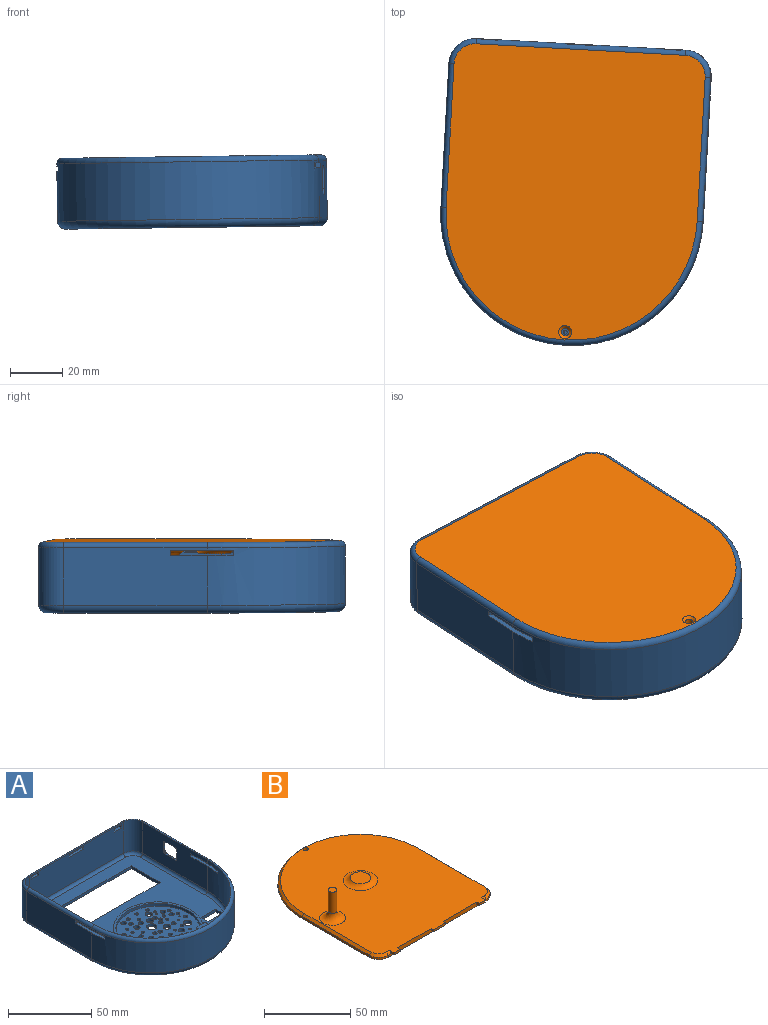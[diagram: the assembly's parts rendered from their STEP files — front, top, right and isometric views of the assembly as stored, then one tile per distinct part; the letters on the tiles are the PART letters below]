
ASSEMBLY  parts=2 mates=1
PART A: 165 faces, bbox 108.2x119.9x27 mm
  f0: plane 55x22mm, normal (1,0,0), area 1042.4mm2, adj f7,f86,f101,f102,f103,f126,f132,f146
  f1: plane 55x23mm, normal (-1,0,0), area 1138.9mm2, adj f8,f92,f101,f102,f103,f120,f132,f138
  f2: plane 20x1.61mm, normal (1,0,0), area 32.1mm2, adj f116,f159,f162,f163
  f3: plane 20x4mm, normal (0,1,0), area 80mm2, adj f116,f156,f159,f160
  f4: plane 20x1.61mm, normal (-1,0,0), area 32.1mm2, adj f116,f154,f156,f157
  f5: plane 80x22mm, normal (0,1,0), area 1733mm2, adj f14,f86,f105,f106,f107,f109,f110,f111
  f6: plane 80x23mm, normal (0,-1,0), area 1789mm2, adj f91,f92,f104,f105,f106,f107,f108,f109
  f7: cylinder r=50mm len=100mm, axis (0,0,-1), area 3415.5mm2, adj f0,f15,f96,f98,f99,f100,f101,f103
  f8: cylinder r=48mm len=96mm, axis (0,0,-1), area 3176.9mm2, adj f1,f9,f96,f98,f99,f100,f101,f103
  f9: plane 55x23mm, normal (1,0,0), area 1237mm2, adj f8,f91,f96,f97,f98,f124,f136
  f10: plane 50.8x50.8mm, normal (0,0,1), area 1631.9mm2, adj f20,f21,f22,f23,f24,f25,f26,f27
  f11: plane 12.3x2mm, normal (0,-1,0), area 24.6mm2, adj f12,f88,f89,f90
  f12: plane 5.9x2mm, normal (-1,0,0), area 11.8mm2, adj f11,f13,f89,f90
  f13: plane 12.3x2mm, normal (0,1,0), area 24.6mm2, adj f12,f88,f89,f90
  f14: cylinder r=10mm len=22mm, axis (0,0,-1), area 345.6mm2, adj f5,f15,f131,f137
  f15: plane 55x22mm, normal (-1,0,0), area 1182mm2, adj f7,f14,f96,f97,f98,f130,f136
  f16: plane 24.5x2mm, normal (1,0,0), area 49mm2, adj f17,f87,f89,f90
  f17: plane 72x2mm, normal (0,-1,0), area 144mm2, adj f16,f18,f89,f90
  f18: plane 24.5x2mm, normal (-1,0,0), area 49mm2, adj f17,f87,f89,f90
  f19: cylinder r=2.5mm len=5mm, axis (0,0,-1), area 31.4mm2, adj f89,f90
  f20: cylinder r=1.09mm len=2.19mm, axis (0,0,-1), area 13.7mm2, adj f10,f90
  f21: cylinder r=1.17mm len=2.34mm, axis (0,0,-1), area 14.7mm2, adj f10,f90
  f22: cylinder r=1.2mm len=2.41mm, axis (0,0,-1), area 15.1mm2, adj f10,f90
  f23: cylinder r=1.12mm len=2.25mm, axis (0,0,-1), area 14.1mm2, adj f10,f90
  f24: cylinder r=1.29mm len=2.57mm, axis (0,0,-1), area 16.2mm2, adj f10,f90
  f25: cylinder r=1.3mm len=2.59mm, axis (0,0,-1), area 16.3mm2, adj f10,f90
  f26: cylinder r=1.3mm len=2.6mm, axis (0,0,-1), area 16.3mm2, adj f10,f90
  f27: cylinder r=1.66mm len=3.33mm, axis (0,0,-1), area 20.9mm2, adj f10,f90
  f28: cylinder r=1.03mm len=2.06mm, axis (0,0,-1), area 12.9mm2, adj f10,f90
  f29: cylinder r=3.5mm len=7mm, axis (0,0,-1), area 44mm2, adj f89,f90
  f30: cylinder r=0.84mm len=2mm, axis (0,0,-1), area 10.6mm2, adj f10,f90
  f31: cylinder r=1.27mm len=2.54mm, axis (0,0,-1), area 15.9mm2, adj f10,f90
  f32: cylinder r=1.09mm len=2.19mm, axis (0,0,-1), area 13.7mm2, adj f10,f90
  f33: cylinder r=1.31mm len=2.61mm, axis (0,0,-1), area 16.4mm2, adj f10,f90
  f34: cylinder r=0.98mm len=2mm, axis (0,0,-1), area 12.3mm2, adj f10,f90
  f35: cylinder r=0.96mm len=2mm, axis (0,0,-1), area 12mm2, adj f10,f90
  f36: cylinder r=1.35mm len=2.7mm, axis (0,0,-1), area 17mm2, adj f10,f90
  f37: cylinder r=0.94mm len=2mm, axis (0,0,-1), area 11.8mm2, adj f10,f90
  f38: cylinder r=2.4mm len=4.79mm, axis (0,0,-1), area 30.1mm2, adj f10,f90
  f39: cylinder r=1.14mm len=2.28mm, axis (0,0,-1), area 14.3mm2, adj f10,f90
  f40: cylinder r=1.19mm len=2.38mm, axis (0,0,-1), area 15mm2, adj f10,f90
  f41: cylinder r=1.46mm len=2.91mm, axis (0,0,-1), area 18.3mm2, adj f10,f90
  f42: cylinder r=1.28mm len=2.56mm, axis (0,0,-1), area 16.1mm2, adj f10,f90
  f43: cylinder r=1.34mm len=2.69mm, axis (0,0,-1), area 16.9mm2, adj f10,f90
  f44: cylinder r=0.79mm len=2mm, axis (0,0,-1), area 9.9mm2, adj f10,f90
  f45: cylinder r=1.96mm len=3.93mm, axis (0,0,-1), area 24.7mm2, adj f10,f90
  f46: cylinder r=1.15mm len=2.3mm, axis (0,0,-1), area 14.5mm2, adj f10,f90
  f47: cylinder r=0.9mm len=2mm, axis (0,0,-1), area 11.3mm2, adj f10,f90
  f48: cylinder r=1.91mm len=3.83mm, axis (0,0,-1), area 24mm2, adj f10,f90
  f49: cylinder r=1.3mm len=2.6mm, axis (0,0,-1), area 16.3mm2, adj f10,f90
  f50: cylinder r=1.04mm len=2.07mm, axis (0,0,-1), area 13mm2, adj f10,f90
  f51: cylinder r=0.35mm len=2mm, axis (0,0,-1), area 4.4mm2, adj f10,f90
  f52: cylinder r=1.46mm len=2.92mm, axis (0,0,-1), area 18.3mm2, adj f10,f90
  f53: cylinder r=0.89mm len=2mm, axis (0,0,-1), area 11.2mm2, adj f10,f90
  f54: cylinder r=1.49mm len=2.98mm, axis (0,0,-1), area 18.7mm2, adj f10,f90
  f55: cylinder r=1.02mm len=2.04mm, axis (0,0,-1), area 12.8mm2, adj f10,f90
  f56: cylinder r=1.22mm len=2.44mm, axis (0,0,-1), area 15.4mm2, adj f10,f90
  f57: cylinder r=1.36mm len=2.73mm, axis (0,0,-1), area 17.1mm2, adj f10,f90
  f58: cylinder r=1.37mm len=2.74mm, axis (0,0,-1), area 17.2mm2, adj f10,f90
  f59: cylinder r=2.62mm len=5.23mm, axis (0,0,-1), area 32.9mm2, adj f10,f90
  f60: cylinder r=0.95mm len=2mm, axis (0,0,-1), area 11.9mm2, adj f10,f90
  f61: cylinder r=1.1mm len=2.2mm, axis (0,0,-1), area 13.8mm2, adj f10,f90
  f62: cylinder r=1.18mm len=2.37mm, axis (0,0,-1), area 14.9mm2, adj f10,f90
  f63: cylinder r=0.85mm len=2mm, axis (0,0,-1), area 10.7mm2, adj f10,f90
  f64: cylinder r=1.19mm len=2.38mm, axis (0,0,-1), area 14.9mm2, adj f10,f90
  f65: cylinder r=0.96mm len=2mm, axis (0,0,-1), area 12mm2, adj f10,f90
  f66: cylinder r=1.7mm len=3.4mm, axis (0,0,-1), area 21.3mm2, adj f10,f90
  f67: cylinder r=0.78mm len=2mm, axis (0,0,-1), area 9.8mm2, adj f10,f90
  f68: cylinder r=0.8mm len=2mm, axis (0,0,-1), area 10.1mm2, adj f10,f90
  f69: cylinder r=1.68mm len=3.36mm, axis (0,0,-1), area 21.1mm2, adj f10,f90
  f70: cylinder r=0.69mm len=2mm, axis (0,0,-1), area 8.7mm2, adj f10,f90
  f71: cylinder r=1.23mm len=2.46mm, axis (0,0,-1), area 15.4mm2, adj f10,f90
  f72: cylinder r=0.88mm len=2mm, axis (0,0,-1), area 11mm2, adj f10,f90
  f73: cylinder r=1.53mm len=3.05mm, axis (0,0,-1), area 19.2mm2, adj f10,f90
  f74: cylinder r=0.9mm len=2mm, axis (0,0,-1), area 11.3mm2, adj f10,f90
  f75: cylinder r=0.63mm len=2mm, axis (0,0,-1), area 7.9mm2, adj f10,f90
  f76: cylinder r=1.17mm len=2.33mm, axis (0,0,-1), area 14.7mm2, adj f10,f90
  f77: cylinder r=1.62mm len=3.25mm, axis (0,0,-1), area 20.4mm2, adj f10,f90
  f78: cylinder r=2.15mm len=4.3mm, axis (0,0,-1), area 27mm2, adj f10,f90
  f79: cylinder r=1.51mm len=3.02mm, axis (0,0,-1), area 19mm2, adj f10,f90
  f80: cylinder r=1.34mm len=2.68mm, axis (0,0,-1), area 16.8mm2, adj f10,f90
  f81: cylinder r=2.36mm len=4.72mm, axis (0,0,-1), area 29.6mm2, adj f10,f90
  f82: cylinder r=3.06mm len=6.12mm, axis (0,0,-1), area 38.5mm2, adj f10,f90
  f83: cylinder r=2.12mm len=4.25mm, axis (0,0,-1), area 26.7mm2, adj f10,f90
  f84: cylinder r=1.85mm len=3.7mm, axis (0,0,-1), area 23.2mm2, adj f10,f90
  f85: cylinder r=1mm len=2mm, axis (0,0,-1), area 12.6mm2, adj f10,f90
  f86: cylinder r=10mm len=22mm, axis (0,0,-1), area 345.6mm2, adj f0,f5,f127,f133
  f87: plane 72x2mm, normal (0,1,0), area 144mm2, adj f16,f18,f89,f90
  f88: plane 5.9x2mm, normal (1,0,0), area 11.8mm2, adj f11,f13,f89,f90
  f89: plane 106.61x92mm, normal (0,0,1), area 4688.8mm2, adj f11,f12,f13,f16,f17,f18,f19,f29
  f90: plane 109x94mm, normal (0,0,-1), area 6987.2mm2, adj f11,f12,f13,f16,f17,f18,f19,f20
  f91: cylinder r=8mm len=23mm, axis (0,0,-1), area 289mm2, adj f6,f9,f123,f137
  f92: cylinder r=8mm len=23mm, axis (0,0,-1), area 289mm2, adj f1,f6,f121,f133
  f93: cylinder r=25.4mm len=50.8mm, axis (0,0,-1), area 319.2mm2, adj f10,f95
  f94: cylinder r=26.9mm len=53.8mm, axis (0,0,-1), area 338mm2, adj f89,f95
  f95: plane 53.8x53.8mm, normal (0,0,1), area 246.5mm2, adj f93,f94
  f96: plane 24x3.05mm, normal (0,0,1), area 48.1mm2, adj f7,f8,f9,f15,f97,f99
  f97: plane 2x2mm, normal (0,-1,0), area 4mm2, adj f9,f15,f96,f98
  f98: plane 24x3.05mm, normal (0,0,-1), area 48.1mm2, adj f7,f8,f9,f15,f97,f99
  f99: plane 2.04x2mm, normal (0,1,0), area 4.1mm2, adj f7,f8,f96,f98
  f100: plane 2.04x2mm, normal (0,1,0), area 4.1mm2, adj f7,f8,f101,f103
  f101: plane 24x3.05mm, normal (0,0,-1), area 48.1mm2, adj f0,f1,f7,f8,f100,f102
  f102: plane 2x2mm, normal (0,-1,0), area 4mm2, adj f0,f1,f101,f103
  f103: plane 24x3.05mm, normal (0,0,1), area 48.1mm2, adj f0,f1,f7,f8,f100,f102
  f104: plane 12x1.73mm, normal (0,0,-1), area 20.8mm2, adj f6,f105,f107,f135
  f105: plane 2x2mm, normal (-1,0,0), area 3.9mm2, adj f5,f6,f104,f106,f135
  f106: plane 12x2mm, normal (0,0,1), area 24mm2, adj f5,f6,f105,f107
  f107: plane 2x2mm, normal (1,0,0), area 3.9mm2, adj f5,f6,f104,f106,f135
  f108: plane 6x1.73mm, normal (0,0,-1), area 10.4mm2, adj f6,f109,f111,f135
  f109: plane 2.5x2mm, normal (-1,0,0), area 4.9mm2, adj f5,f6,f108,f110,f135
  f110: plane 6x2mm, normal (0,0,1), area 12mm2, adj f5,f6,f109,f111
  f111: plane 2.5x2mm, normal (1,0,0), area 4.9mm2, adj f5,f6,f108,f110,f135
  f112: plane 6x1.73mm, normal (0,0,-1), area 10.4mm2, adj f6,f113,f115,f135
  f113: plane 2x2mm, normal (-1,0,0), area 3.9mm2, adj f5,f6,f112,f114,f135
  f114: plane 6x2mm, normal (0,0,1), area 12mm2, adj f5,f6,f113,f115
  f115: plane 2x2mm, normal (1,0,0), area 3.9mm2, adj f5,f6,f112,f114,f135
  f116: plane 12.52x6mm, normal (0,0,1), area 46.3mm2, adj f2,f3,f4,f8,f118,f154,f156,f159
  f117: plane 1.5x1.5mm, normal (0,0,1), area 1.8mm2, adj f118
  f118: cylinder r=0.75mm len=22mm, axis (0,0,-1), area 103.7mm2, adj f116,f117
  f119: torus R=46mm, axis (0,0,1), area 213.9mm2, adj f8,f89,f120,f164
  f120: cylinder r=2mm len=55mm, axis (0,-1,0), area 172.8mm2, adj f1,f89,f119,f121
  f121: torus R=6mm, axis (0,0,1), area 35.9mm2, adj f89,f92,f120,f122
  f122: cylinder r=2mm len=80mm, axis (1,0,0), area 251.3mm2, adj f6,f89,f121,f123
  f123: torus R=6mm, axis (0,0,1), area 35.9mm2, adj f89,f91,f122,f124
  f124: cylinder r=2mm len=55mm, axis (0,1,0), area 172.8mm2, adj f9,f89,f123,f125
  f125: torus R=46mm, axis (0,0,1), area 213.9mm2, adj f8,f89,f124,f155
  f126: cylinder r=3mm len=55mm, axis (0,1,0), area 259.2mm2, adj f0,f90,f127,f128
  f127: torus R=7mm, axis (0,0,1), area 66mm2, adj f86,f90,f126,f129
  f128: torus R=47mm, axis (0,0,1), area 724.1mm2, adj f7,f90,f126,f130
  f129: cylinder r=3mm len=80mm, axis (-1,0,0), area 377mm2, adj f5,f90,f127,f131
  f130: cylinder r=3mm len=55mm, axis (0,-1,0), area 259.2mm2, adj f15,f90,f128,f131
  f131: torus R=7mm, axis (0,0,1), area 66mm2, adj f14,f90,f129,f130
  f132: cylinder r=2mm len=55mm, axis (0,-1,0), area 172.8mm2, adj f0,f1,f133,f134
  f133: torus R=8mm, axis (0,0,1), area 45.8mm2, adj f86,f92,f132,f135
  f134: torus R=48mm, axis (0,0,1), area 486.3mm2, adj f7,f8,f132,f136
  f135: cylinder r=2mm len=80mm, axis (1,0,0), area 226.2mm2, adj f5,f6,f104,f105,f107,f108,f109,f111
  f136: cylinder r=2mm len=55mm, axis (0,1,0), area 172.8mm2, adj f9,f15,f134,f137
  f137: torus R=8mm, axis (0,0,1), area 45.8mm2, adj f14,f91,f135,f136
  f138: plane 9x1mm, normal (0,0,-1), area 9mm2, adj f1,f142,f145,f153
  f139: plane 7x1mm, normal (0,1,0), area 7mm2, adj f1,f142,f143,f149
  f140: plane 9x1mm, normal (0,0,1), area 9mm2, adj f1,f143,f144,f146
  f141: plane 7x1mm, normal (0,-1,0), area 7mm2, adj f1,f144,f145,f150
  f142: cylinder r=1mm len=1mm, axis (1,0,0), area 1.6mm2, adj f1,f138,f139,f151
  f143: cylinder r=1mm len=1mm, axis (-1,0,0), area 1.6mm2, adj f1,f139,f140,f147
  f144: cylinder r=1mm len=1mm, axis (1,0,0), area 1.6mm2, adj f1,f140,f141,f148
  f145: cylinder r=1mm len=1mm, axis (-1,0,0), area 1.6mm2, adj f1,f138,f141,f152
  f146: plane 9x1mm, normal (0.71,0,0.71), area 12.7mm2, adj f0,f140,f147,f148
  f147: cone r=2mm half-angle=45deg, axis (1,0,0), area 3.3mm2, adj f0,f143,f146,f149
  f148: cone r=2mm half-angle=45deg, axis (1,0,0), area 3.3mm2, adj f0,f144,f146,f150
  f149: plane 7x1mm, normal (0.71,0.71,0), area 9.9mm2, adj f0,f139,f147,f151
  f150: plane 7x1mm, normal (0.71,-0.71,0), area 9.9mm2, adj f0,f141,f148,f152
  f151: cone r=2mm half-angle=45deg, axis (1,0,0), area 3.3mm2, adj f0,f142,f149,f153
  f152: cone r=2mm half-angle=45deg, axis (1,0,0), area 3.3mm2, adj f0,f145,f150,f153
  f153: plane 9x1mm, normal (0.71,0,-0.71), area 12.7mm2, adj f0,f138,f151,f152
  f154: cylinder r=2mm len=20mm, axis (0,0,-1), area 68.1mm2, adj f4,f8,f116,f155
  f155: sphere r=2mm, area 6.8mm2, adj f125,f154,f157
  f156: cylinder r=2mm len=20mm, axis (0,0,1), area 62.8mm2, adj f3,f4,f116,f158
  f157: cylinder r=2mm len=2mm, axis (0,-1,0), area 5mm2, adj f4,f89,f155,f158
  f158: torus R=4mm, axis (0,0,1), area 13.5mm2, adj f89,f156,f157,f160
  f159: cylinder r=2mm len=20mm, axis (0,0,-1), area 62.8mm2, adj f2,f3,f116,f161
  f160: cylinder r=2mm len=4mm, axis (-1,0,0), area 12.6mm2, adj f3,f89,f158,f161
  f161: torus R=4mm, axis (0,0,1), area 13.5mm2, adj f89,f159,f160,f163
  f162: cylinder r=2mm len=20mm, axis (0,0,-1), area 68.1mm2, adj f2,f8,f116,f164
  f163: cylinder r=2mm len=2mm, axis (0,1,0), area 5mm2, adj f2,f89,f161,f164
  f164: sphere r=2mm, area 6.8mm2, adj f119,f162,f163
PART B: 34 faces, bbox 98x113x23 mm
  f0: plane 2x1.5mm, normal (-1,0,0), area 3mm2, adj f7,f16,f17,f24
  f1: plane 2x1.5mm, normal (1,0,0), area 3mm2, adj f7,f16,f17,f24
  f2: plane 2x1.5mm, normal (-1,0,0), area 3mm2, adj f8,f16,f17,f23
  f3: plane 3.5x1.5mm, normal (1,0,0), area 4.1mm2, adj f8,f17,f23,f33
  f4: plane 3.5x1.5mm, normal (-1,0,0), area 4.1mm2, adj f14,f17,f25,f27
  f5: plane 2x1.5mm, normal (1,0,0), area 3mm2, adj f14,f16,f17,f25
  f6: plane 111x96mm, normal (0,0,-1), area 9620mm2, adj f9,f10,f11,f12,f13,f16,f26
  f7: plane 10x1.5mm, normal (0,-1,0), area 15mm2, adj f0,f1,f17,f24
  f8: plane 5x1.5mm, normal (0,-1,0), area 7.5mm2, adj f2,f3,f17,f23
  f9: cylinder r=8mm len=8mm, axis (0,0,-1), area 18.8mm2, adj f6,f10,f16,f32
  f10: plane 55x1.5mm, normal (1,0,0), area 82.5mm2, adj f6,f9,f11,f31
  f11: cylinder r=48mm len=96mm, axis (0,0,-1), area 226.2mm2, adj f6,f10,f12,f30
  f12: plane 55x1.5mm, normal (-1,0,0), area 82.5mm2, adj f6,f11,f13,f29
  f13: cylinder r=8mm len=8mm, axis (0,0,-1), area 18.8mm2, adj f6,f12,f16,f28
  f14: plane 5x1.5mm, normal (0,-1,0), area 7.5mm2, adj f4,f5,f17,f25
  f15: cylinder r=1.5mm len=3mm, axis (0,0,-1), area 18.8mm2, adj f17,f26
  f16: plane 80x3mm, normal (0,-1,0), area 202.5mm2, adj f0,f1,f2,f5,f6,f9,f13,f17
  f17: plane 111.5x93mm, normal (0,0,1), area 8752.4mm2, adj f0,f1,f2,f3,f4,f5,f7,f8
  f18: plane 12x12mm, normal (0,0,1), area 113.1mm2, adj f19
  f19: torus R=10mm, axis (0,0,1), area 228.5mm2, adj f17,f18
  f20: cylinder r=2.5mm len=15mm, axis (0,0,-1), area 235.6mm2, adj f21,f22
  f21: plane 5x5mm, normal (0,0,1), area 19.6mm2, adj f20
  f22: torus R=7.5mm, axis (0,0,1), area 213mm2, adj f17,f20
  f23: plane 5x2mm, normal (0,0,-1), area 10mm2, adj f2,f3,f8,f16
  f24: plane 10x2mm, normal (0,0,-1), area 20mm2, adj f0,f1,f7,f16
  f25: plane 5x2mm, normal (0,0,-1), area 10mm2, adj f4,f5,f14,f16
  f26: cone r=2.5mm half-angle=45deg, axis (0,0,-1), area 17.8mm2, adj f6,f15
  f27: plane 2.5x1.5mm, normal (0,-0.71,0.71), area 5.3mm2, adj f4,f16,f17,f28
  f28: cone r=6.5mm half-angle=45deg, axis (0,0,-1), area 24.2mm2, adj f13,f17,f27,f29
  f29: plane 55x1.5mm, normal (-0.71,0,0.71), area 116.7mm2, adj f12,f17,f28,f30
  f30: cone r=46.5mm half-angle=45deg, axis (0,0,-1), area 314.9mm2, adj f11,f17,f29,f31
  f31: plane 55x1.5mm, normal (0.71,0,0.71), area 116.7mm2, adj f10,f17,f30,f32
  f32: cone r=6.5mm half-angle=45deg, axis (0,0,-1), area 24.2mm2, adj f9,f17,f31,f33
  f33: plane 2.5x1.5mm, normal (0,-0.71,0.71), area 5.3mm2, adj f3,f16,f17,f32
PLACE A rot(axis=(-0.01,-0.24,-0.97),3.3deg) t=(-23.03,2.53,80.49)mm
PLACE B rot(axis=(1,-0.03,0.01),180deg) t=(-23.12,7.54,107.48)mm
MATE fastened A.f106 <-> B.f17  axis (-0.01,0,1) through (-19.5,72.44,104.48)mm
